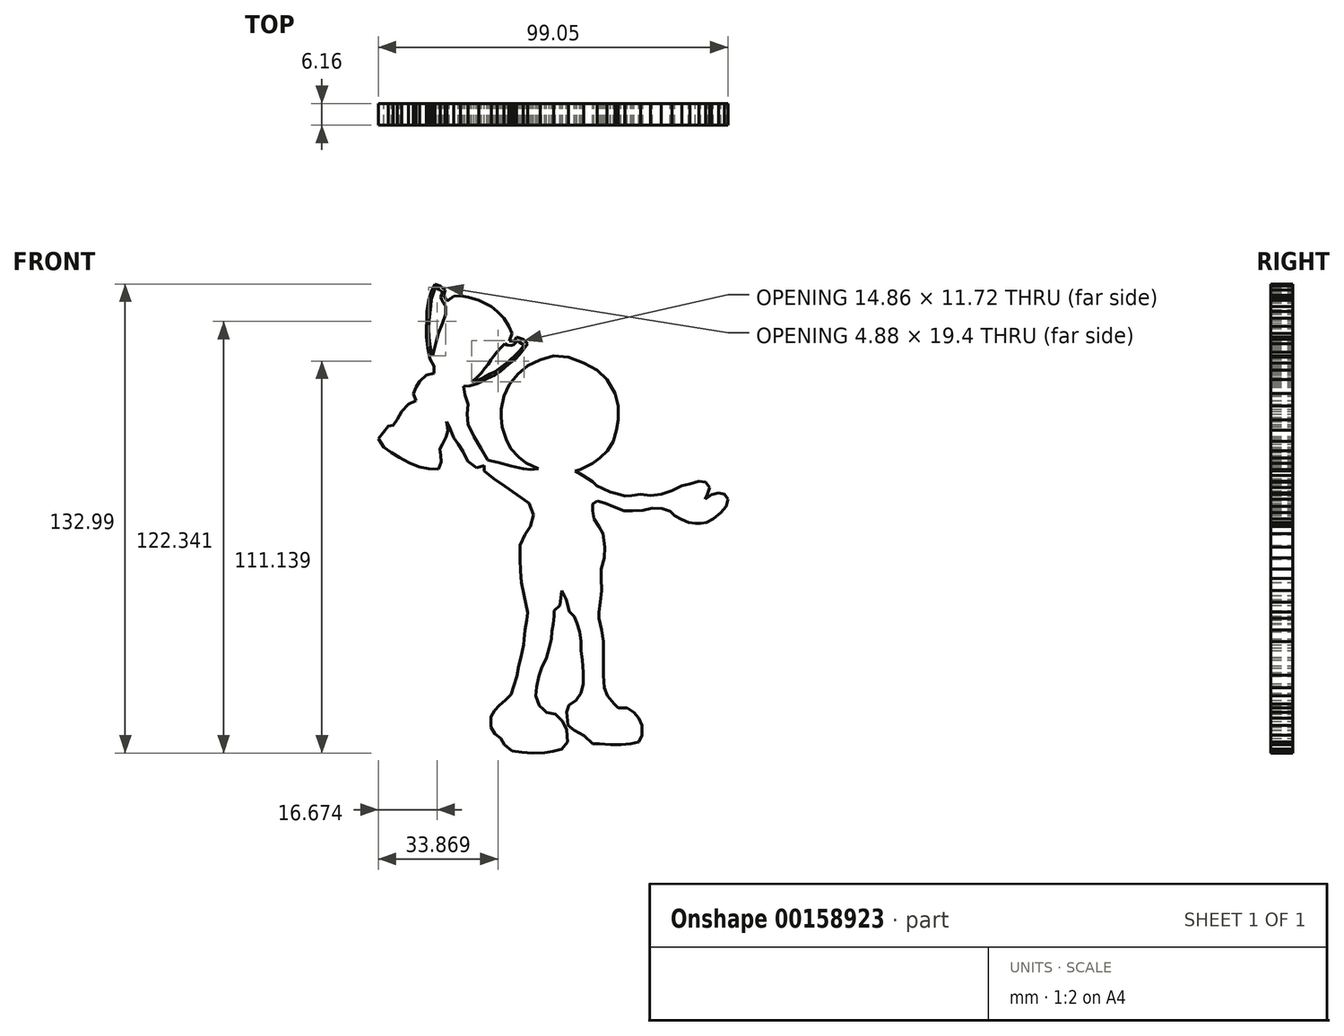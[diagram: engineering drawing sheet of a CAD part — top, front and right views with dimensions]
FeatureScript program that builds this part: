
annotation { "Feature Type Name" : "Feature", "Feature Type Description" : "" }
export const myFeature = defineFeature(function(context is Context, id is Id, definition is map)
    precondition{}
    {
        {
            var Q0;
            Q0=qCreatedBy(makeId("Front.planeOp"),FACE);
            var sketch = newSketch(context, id + "F0", { "sketchPlane" : qUnion([Q0])});
            skLineSegment(sketch, "E0", {"start": v(-2.87, 14.43) * mm, "end": v(0, 12.63) * mm});
            skPoint(sketch, "E1", {"position": v(-19.71, 16.4) * mm});
            skPoint(sketch, "E2", {"position": v(-23.12, 17.11) * mm});
            skPoint(sketch, "E3", {"position": v(-26.88, 18.19) * mm});
            skPoint(sketch, "E4", {"position": v(-29.75, 18.73) * mm});
            skPoint(sketch, "E5", {"position": v(-31.72, 22.13) * mm});
            skPoint(sketch, "E6", {"position": v(-33.69, 25.54) * mm});
            skPoint(sketch, "E7", {"position": v(-35.3, 28.94) * mm});
            skPoint(sketch, "E8", {"position": v(-35.66, 31.8) * mm});
            skPoint(sketch, "E9", {"position": v(-35.3, 34.67) * mm});
            skPoint(sketch, "E10", {"position": v(-36.2, 37.36) * mm});
            skPoint(sketch, "E11", {"position": v(-36.56, 39.7) * mm});
            skPoint(sketch, "E12", {"position": v(-41.04, 27.15) * mm});
            skPoint(sketch, "E13", {"position": v(-39.42, 25.18) * mm});
            skPoint(sketch, "E14", {"position": v(-38.17, 23.38) * mm});
            skPoint(sketch, "E15", {"position": v(-36.73, 21.23) * mm});
            skPoint(sketch, "E16", {"position": v(-35.48, 18.55) * mm});
            skPoint(sketch, "E17", {"position": v(-32.97, 16.58) * mm});
            skPoint(sketch, "E18", {"position": v(-30.82, 17.3) * mm});
            skPoint(sketch, "E19", {"position": v(-30.82, 15.68) * mm});
            skPoint(sketch, "E20", {"position": v(-28.13, 13.53) * mm});
            skPoint(sketch, "E21", {"position": v(-24.9, 11.38) * mm});
            skPoint(sketch, "E22", {"position": v(-21.5, 9.05) * mm});
            skPoint(sketch, "E23", {"position": v(-18.1, 6.54) * mm});
            skPoint(sketch, "E24", {"position": v(-16.84, 3.32) * mm});
            skPoint(sketch, "E25", {"position": v(-17.74, 0) * mm});
            skPoint(sketch, "E26", {"position": v(-19.17, -2.24) * mm});
            skPoint(sketch, "E27", {"position": v(-20.6, -5.29) * mm});
            skPoint(sketch, "E28", {"position": v(-20.6, -9.23) * mm});
            skPoint(sketch, "E29", {"position": v(-20.43, -12.63) * mm});
            skPoint(sketch, "E30", {"position": v(-20.25, -15.86) * mm});
            skPoint(sketch, "E31", {"position": v(-19.53, -19.62) * mm});
            skPoint(sketch, "E32", {"position": v(-18.46, -24.46) * mm});
            skPoint(sketch, "E33", {"position": v(-16.13, -24.46) * mm});
            skPoint(sketch, "E34", {"position": v(-13.62, -23.92) * mm});
            skPoint(sketch, "E35", {"position": v(-10.93, -23.92) * mm});
            skPoint(sketch, "E36", {"position": v(-9.32, -22.3) * mm});
            skPoint(sketch, "E37", {"position": v(-8.78, -18.19) * mm});
            skPoint(sketch, "E38", {"position": v(-7.53, -20.7) * mm});
            skPoint(sketch, "E39", {"position": v(-6.63, -24.1) * mm});
            skPoint(sketch, "E40", {"position": v(-5.2, -25.54) * mm});
            skPoint(sketch, "E41", {"position": v(-3.4, -24.64) * mm});
            skPoint(sketch, "E42", {"position": v(0, -24.1) * mm});
            skPoint(sketch, "E43", {"position": v(1.8, -24.28) * mm});
            skPoint(sketch, "E44", {"position": v(2.15, -21.41) * mm});
            skPoint(sketch, "E45", {"position": v(2.5, -18.19) * mm});
            skPoint(sketch, "E46", {"position": v(2.33, -14.78) * mm});
            skPoint(sketch, "E47", {"position": v(2.33, -12.1) * mm});
            skPoint(sketch, "E48", {"position": v(3.23, -8.87) * mm});
            skPoint(sketch, "E49", {"position": v(3.4, -5.82) * mm});
            skPoint(sketch, "E50", {"position": v(2.87, -2.06) * mm});
            skPoint(sketch, "E51", {"position": v(1.7, 0) * mm});
            skPoint(sketch, "E52", {"position": v(0, 4.38) * mm});
            skPoint(sketch, "E53", {"position": v(0, 6.38) * mm});
            skPoint(sketch, "E54", {"position": v(1.19, 7.18) * mm});
            skPoint(sketch, "E55", {"position": v(3.49, 6.58) * mm});
            skPoint(sketch, "E56", {"position": v(5.99, 5.58) * mm});
            skPoint(sketch, "E57", {"position": v(7.99, 5.38) * mm});
            skPoint(sketch, "E58", {"position": v(7.99, 6.98) * mm});
            skPoint(sketch, "E59", {"position": v(9.09, 8.58) * mm});
            skPoint(sketch, "E60", {"position": v(8.89, 4.48) * mm});
            skPoint(sketch, "E61", {"position": v(11.29, 4.38) * mm});
            skPoint(sketch, "E62", {"position": v(14.19, 4.58) * mm});
            skPoint(sketch, "E63", {"position": v(16.89, 5.18) * mm});
            skPoint(sketch, "E64", {"position": v(19.69, 5.08) * mm});
            skPoint(sketch, "E65", {"position": v(21.89, 4.28) * mm});
            skPoint(sketch, "E66", {"position": v(23.19, 3.08) * mm});
            skPoint(sketch, "E67", {"position": v(25.09, 2.08) * mm});
            skPoint(sketch, "E68", {"position": v(27.09, 1.18) * mm});
            skPoint(sketch, "E69", {"position": v(1.09, 11.58) * mm});
            skPoint(sketch, "E70", {"position": v(2.79, 10.78) * mm});
            skPoint(sketch, "E71", {"position": v(4.89, 9.78) * mm});
            skPoint(sketch, "E72", {"position": v(6.89, 9.28) * mm});
            skPoint(sketch, "E73", {"position": v(10.99, 8.78) * mm});
            skPoint(sketch, "E74", {"position": v(13.59, 9.08) * mm});
            skPoint(sketch, "E75", {"position": v(16.39, 8.78) * mm});
            skPoint(sketch, "E76", {"position": v(19.39, 9.08) * mm});
            skPoint(sketch, "E77", {"position": v(22.49, 10.18) * mm});
            skPoint(sketch, "E78", {"position": v(25.19, 11.58) * mm});
            skPoint(sketch, "E79", {"position": v(27.49, 12.08) * mm});
            skPoint(sketch, "E80", {"position": v(30.09, 12.78) * mm});
            skPoint(sketch, "E81", {"position": v(31.99, 12.58) * mm});
            skPoint(sketch, "E82", {"position": v(33.09, 10.98) * mm});
            skPoint(sketch, "E83", {"position": v(32.49, 9.18) * mm});
            skPoint(sketch, "E84", {"position": v(30.69, 7.78) * mm});
            skPoint(sketch, "E85", {"position": v(29.49, 8.48) * mm});
            skPoint(sketch, "E86", {"position": v(31.89, 7.78) * mm});
            skPoint(sketch, "E87", {"position": v(33.59, 8.98) * mm});
            skPoint(sketch, "E88", {"position": v(35.69, 9.48) * mm});
            skPoint(sketch, "E89", {"position": v(37.29, 9.08) * mm});
            skPoint(sketch, "E90", {"position": v(38.29, 7.68) * mm});
            skPoint(sketch, "E91", {"position": v(37.79, 5.68) * mm});
            skPoint(sketch, "E92", {"position": v(36.29, 3.98) * mm});
            skPoint(sketch, "E93", {"position": v(34.19, 2.18) * mm});
            skPoint(sketch, "E94", {"position": v(32.19, 1.18) * mm});
            skPoint(sketch, "E95", {"position": v(28.99, 0.88) * mm});
            skPoint(sketch, "E96", {"position": v(30.59, 0.88) * mm});
            skPoint(sketch, "E97", {"position": v(-18.76, -26.6) * mm});
            skPoint(sketch, "E98", {"position": v(-19.26, -29.3) * mm});
            skPoint(sketch, "E99", {"position": v(-19.46, -32) * mm});
            skPoint(sketch, "E100", {"position": v(-19.56, -33.5) * mm});
            skPoint(sketch, "E101", {"position": v(-20.36, -37.09) * mm});
            skPoint(sketch, "E102", {"position": v(-20.96, -39.48) * mm});
            skPoint(sketch, "E103", {"position": v(-21.45, -42.48) * mm});
            skPoint(sketch, "E104", {"position": v(-22.35, -45.28) * mm});
            skPoint(sketch, "E105", {"position": v(-23.15, -47.67) * mm});
            skPoint(sketch, "E106", {"position": v(-24.75, -49.27) * mm});
            skPoint(sketch, "E107", {"position": v(-26.45, -50.67) * mm});
            skPoint(sketch, "E108", {"position": v(-27.85, -52.27) * mm});
            skPoint(sketch, "E109", {"position": v(-28.84, -53.96) * mm});
            skPoint(sketch, "E110", {"position": v(-28.84, -56.86) * mm});
            skPoint(sketch, "E111", {"position": v(-27.75, -58.86) * mm});
            skPoint(sketch, "E112", {"position": v(-26.05, -60.05) * mm});
            skPoint(sketch, "E113", {"position": v(-25.05, -61.85) * mm});
            skPoint(sketch, "E114", {"position": v(-22.85, -63.65) * mm});
            skPoint(sketch, "E115", {"position": v(-20.16, -64.05) * mm});
            skPoint(sketch, "E116", {"position": v(-17.06, -64.25) * mm});
            skPoint(sketch, "E117", {"position": v(-13.67, -64.15) * mm});
            skPoint(sketch, "E118", {"position": v(-11.37, -63.75) * mm});
            skPoint(sketch, "E119", {"position": v(-8.77, -63.15) * mm});
            skPoint(sketch, "E120", {"position": v(-7.18, -61.15) * mm});
            skPoint(sketch, "E121", {"position": v(-7.38, -57.66) * mm});
            skPoint(sketch, "E122", {"position": v(-8.57, -55.26) * mm});
            skPoint(sketch, "E123", {"position": v(-10.57, -53.26) * mm});
            skPoint(sketch, "E124", {"position": v(-13.17, -52.77) * mm});
            skPoint(sketch, "E125", {"position": v(-14.07, -51.87) * mm});
            skPoint(sketch, "E126", {"position": v(-15.16, -50.77) * mm});
            skPoint(sketch, "E127", {"position": v(-16.16, -48.07) * mm});
            skPoint(sketch, "E128", {"position": v(-15.96, -45.48) * mm});
            skPoint(sketch, "E129", {"position": v(-15.26, -42.38) * mm});
            skPoint(sketch, "E130", {"position": v(-14.46, -40.08) * mm});
            skPoint(sketch, "E131", {"position": v(-13.07, -37.19) * mm});
            skPoint(sketch, "E132", {"position": v(-12.37, -34.5) * mm});
            skPoint(sketch, "E133", {"position": v(-11.77, -31.9) * mm});
            skPoint(sketch, "E134", {"position": v(-11.27, -27.7) * mm});
            skPoint(sketch, "E135", {"position": v(-10.97, -25.4) * mm});
            skPoint(sketch, "E136", {"position": v(-11.57, -29.7) * mm});
            skPoint(sketch, "E137", {"position": v(-4.48, -27.5) * mm});
            skPoint(sketch, "E138", {"position": v(-3.68, -29.9) * mm});
            skPoint(sketch, "E139", {"position": v(-3.28, -32.5) * mm});
            skPoint(sketch, "E140", {"position": v(-3.38, -35.2) * mm});
            skPoint(sketch, "E141", {"position": v(-2.98, -37.89) * mm});
            skPoint(sketch, "E142", {"position": v(-2.68, -41.38) * mm});
            skPoint(sketch, "E143", {"position": v(-2.68, -44.58) * mm});
            skPoint(sketch, "E144", {"position": v(-3.38, -47.27) * mm});
            skPoint(sketch, "E145", {"position": v(-4.78, -49.27) * mm});
            skPoint(sketch, "E146", {"position": v(-6.78, -50.67) * mm});
            skPoint(sketch, "E147", {"position": v(-7.38, -52.57) * mm});
            skPoint(sketch, "E148", {"position": v(-7.08, -56.36) * mm});
            skPoint(sketch, "E149", {"position": v(-5.28, -57.76) * mm});
            skPoint(sketch, "E150", {"position": v(-2.48, -59.36) * mm});
            skPoint(sketch, "E151", {"position": v(0, -61.65) * mm});
            skPoint(sketch, "E152", {"position": v(1.91, -61.65) * mm});
            skPoint(sketch, "E153", {"position": v(5, -61.85) * mm});
            skPoint(sketch, "E154", {"position": v(7.9, -61.85) * mm});
            skPoint(sketch, "E155", {"position": v(10.8, -61.65) * mm});
            skPoint(sketch, "E156", {"position": v(13.1, -61.05) * mm});
            skPoint(sketch, "E157", {"position": v(14, -59.26) * mm});
            skPoint(sketch, "E158", {"position": v(14, -56.36) * mm});
            skPoint(sketch, "E159", {"position": v(13.1, -54.36) * mm});
            skPoint(sketch, "E160", {"position": v(11.6, -52.67) * mm});
            skPoint(sketch, "E161", {"position": v(9.8, -51.47) * mm});
            skPoint(sketch, "E162", {"position": v(7.2, -51.47) * mm});
            skPoint(sketch, "E163", {"position": v(6, -50.37) * mm});
            skPoint(sketch, "E164", {"position": v(4.2, -48.07) * mm});
            skPoint(sketch, "E165", {"position": v(3.3, -45.78) * mm});
            skPoint(sketch, "E166", {"position": v(3, -42.18) * mm});
            skPoint(sketch, "E167", {"position": v(3, -39.48) * mm});
            skPoint(sketch, "E168", {"position": v(3, -35.79) * mm});
            skPoint(sketch, "E169", {"position": v(3, -32.7) * mm});
            skPoint(sketch, "E170", {"position": v(2.51, -29.3) * mm});
            skPoint(sketch, "E171", {"position": v(1.71, -26.1) * mm});
            skLineSegment(sketch, "E172", {"start": v(0, 12.63) * mm, "end": v(1.09, 11.58) * mm});
            skLineSegment(sketch, "E173", {"start": v(1.09, 11.58) * mm, "end": v(2.79, 10.78) * mm});
            skLineSegment(sketch, "E174", {"start": v(2.79, 10.78) * mm, "end": v(4.89, 9.78) * mm});
            skLineSegment(sketch, "E175", {"start": v(4.89, 9.78) * mm, "end": v(6.89, 9.28) * mm});
            skLineSegment(sketch, "E176", {"start": v(6.89, 9.28) * mm, "end": v(9.09, 8.58) * mm});
            skLineSegment(sketch, "E177", {"start": v(9.09, 8.58) * mm, "end": v(10.99, 8.78) * mm});
            skLineSegment(sketch, "E178", {"start": v(10.99, 8.78) * mm, "end": v(13.59, 9.08) * mm});
            skLineSegment(sketch, "E179", {"start": v(13.59, 9.08) * mm, "end": v(16.39, 8.78) * mm});
            skLineSegment(sketch, "E180", {"start": v(16.39, 8.78) * mm, "end": v(19.39, 9.08) * mm});
            skLineSegment(sketch, "E181", {"start": v(19.39, 9.08) * mm, "end": v(22.49, 10.18) * mm});
            skLineSegment(sketch, "E182", {"start": v(22.49, 10.18) * mm, "end": v(25.19, 11.58) * mm});
            skLineSegment(sketch, "E183", {"start": v(25.19, 11.58) * mm, "end": v(27.49, 12.08) * mm});
            skLineSegment(sketch, "E184", {"start": v(27.49, 12.08) * mm, "end": v(30.09, 12.78) * mm});
            skLineSegment(sketch, "E185", {"start": v(30.09, 12.78) * mm, "end": v(31.99, 12.58) * mm});
            skLineSegment(sketch, "E186", {"start": v(31.99, 12.58) * mm, "end": v(33.09, 10.98) * mm});
            skLineSegment(sketch, "E187", {"start": v(33.09, 10.98) * mm, "end": v(32.49, 9.18) * mm});
            skLineSegment(sketch, "E188", {"start": v(32.49, 9.18) * mm, "end": v(31.89, 7.78) * mm});
            skLineSegment(sketch, "E189", {"start": v(31.89, 7.78) * mm, "end": v(30.69, 7.78) * mm});
            skLineSegment(sketch, "E190", {"start": v(30.69, 7.78) * mm, "end": v(29.49, 8.48) * mm});
            skLineSegment(sketch, "E191", {"start": v(31.89, 7.78) * mm, "end": v(33.59, 8.98) * mm});
            skLineSegment(sketch, "E192", {"start": v(33.59, 8.98) * mm, "end": v(35.69, 9.48) * mm});
            skLineSegment(sketch, "E193", {"start": v(35.69, 9.48) * mm, "end": v(37.29, 9.08) * mm});
            skLineSegment(sketch, "E194", {"start": v(37.29, 9.08) * mm, "end": v(38.29, 7.68) * mm});
            skLineSegment(sketch, "E195", {"start": v(38.29, 7.68) * mm, "end": v(37.79, 5.68) * mm});
            skLineSegment(sketch, "E196", {"start": v(37.79, 5.68) * mm, "end": v(36.29, 3.98) * mm});
            skLineSegment(sketch, "E197", {"start": v(36.29, 3.98) * mm, "end": v(34.19, 2.18) * mm});
            skLineSegment(sketch, "E198", {"start": v(34.19, 2.18) * mm, "end": v(32.19, 1.18) * mm});
            skLineSegment(sketch, "E199", {"start": v(32.19, 1.18) * mm, "end": v(30.59, 0.88) * mm});
            skLineSegment(sketch, "E200", {"start": v(30.59, 0.88) * mm, "end": v(28.99, 0.88) * mm});
            skLineSegment(sketch, "E201", {"start": v(28.99, 0.88) * mm, "end": v(27.09, 1.18) * mm});
            skLineSegment(sketch, "E202", {"start": v(27.09, 1.18) * mm, "end": v(25.09, 2.08) * mm});
            skLineSegment(sketch, "E203", {"start": v(25.09, 2.08) * mm, "end": v(23.19, 3.08) * mm});
            skLineSegment(sketch, "E204", {"start": v(23.19, 3.08) * mm, "end": v(21.89, 4.28) * mm});
            skLineSegment(sketch, "E205", {"start": v(21.89, 4.28) * mm, "end": v(19.69, 5.08) * mm});
            skLineSegment(sketch, "E206", {"start": v(19.69, 5.08) * mm, "end": v(16.89, 5.18) * mm});
            skLineSegment(sketch, "E207", {"start": v(16.89, 5.18) * mm, "end": v(14.19, 4.58) * mm});
            skLineSegment(sketch, "E208", {"start": v(14.19, 4.58) * mm, "end": v(11.29, 4.38) * mm});
            skLineSegment(sketch, "E209", {"start": v(11.29, 4.38) * mm, "end": v(8.89, 4.48) * mm});
            skLineSegment(sketch, "E210", {"start": v(8.89, 4.48) * mm, "end": v(7.99, 5.38) * mm});
            skLineSegment(sketch, "E211", {"start": v(7.99, 5.38) * mm, "end": v(7.99, 6.98) * mm});
            skLineSegment(sketch, "E212", {"start": v(7.99, 6.98) * mm, "end": v(9.09, 8.58) * mm});
            skLineSegment(sketch, "E213", {"start": v(8.89, 4.48) * mm, "end": v(5.99, 5.58) * mm});
            skLineSegment(sketch, "E214", {"start": v(5.99, 5.58) * mm, "end": v(3.49, 6.58) * mm});
            skLineSegment(sketch, "E215", {"start": v(3.49, 6.58) * mm, "end": v(1.19, 7.18) * mm});
            skLineSegment(sketch, "E216", {"start": v(1.19, 7.18) * mm, "end": v(0, 6.38) * mm});
            skLineSegment(sketch, "E217", {"start": v(0, 6.38) * mm, "end": v(0, 4.38) * mm});
            skPoint(sketch, "E218", {"position": v(0.37, 2.2) * mm});
            skLineSegment(sketch, "E219", {"start": v(0, 4.38) * mm, "end": v(0.37, 2.2) * mm});
            skLineSegment(sketch, "E220", {"start": v(0.37, 2.2) * mm, "end": v(1.7, 0) * mm});
            skLineSegment(sketch, "E221", {"start": v(1.7, 0) * mm, "end": v(2.87, -2.06) * mm});
            skLineSegment(sketch, "E222", {"start": v(2.87, -2.06) * mm, "end": v(3.4, -5.82) * mm});
            skLineSegment(sketch, "E223", {"start": v(3.4, -5.82) * mm, "end": v(3.23, -8.87) * mm});
            skLineSegment(sketch, "E224", {"start": v(3.23, -8.87) * mm, "end": v(2.33, -12.1) * mm});
            skLineSegment(sketch, "E225", {"start": v(2.33, -12.1) * mm, "end": v(2.33, -14.78) * mm});
            skLineSegment(sketch, "E226", {"start": v(2.33, -14.78) * mm, "end": v(2.5, -18.19) * mm});
            skLineSegment(sketch, "E227", {"start": v(2.5, -18.19) * mm, "end": v(2.15, -21.41) * mm});
            skLineSegment(sketch, "E228", {"start": v(2.15, -21.41) * mm, "end": v(1.8, -24.28) * mm});
            skLineSegment(sketch, "E229", {"start": v(1.8, -24.28) * mm, "end": v(1.71, -26.1) * mm});
            skLineSegment(sketch, "E230", {"start": v(1.71, -26.1) * mm, "end": v(2.51, -29.3) * mm});
            skLineSegment(sketch, "E231", {"start": v(2.51, -29.3) * mm, "end": v(3, -32.7) * mm});
            skLineSegment(sketch, "E232", {"start": v(3, -32.7) * mm, "end": v(3, -35.79) * mm});
            skLineSegment(sketch, "E233", {"start": v(3, -35.79) * mm, "end": v(3, -39.48) * mm});
            skLineSegment(sketch, "E234", {"start": v(3, -39.48) * mm, "end": v(3, -42.18) * mm});
            skLineSegment(sketch, "E235", {"start": v(3, -42.18) * mm, "end": v(3.3, -45.78) * mm});
            skLineSegment(sketch, "E236", {"start": v(3.3, -45.78) * mm, "end": v(4.2, -48.07) * mm});
            skLineSegment(sketch, "E237", {"start": v(4.2, -48.07) * mm, "end": v(6, -50.37) * mm});
            skLineSegment(sketch, "E238", {"start": v(6, -50.37) * mm, "end": v(7.2, -51.47) * mm});
            skLineSegment(sketch, "E239", {"start": v(7.2, -51.47) * mm, "end": v(9.8, -51.47) * mm});
            skLineSegment(sketch, "E240", {"start": v(9.8, -51.47) * mm, "end": v(11.6, -52.67) * mm});
            skLineSegment(sketch, "E241", {"start": v(11.6, -52.67) * mm, "end": v(13.1, -54.36) * mm});
            skLineSegment(sketch, "E242", {"start": v(13.1, -54.36) * mm, "end": v(14, -56.36) * mm});
            skLineSegment(sketch, "E243", {"start": v(14, -56.36) * mm, "end": v(14, -59.26) * mm});
            skLineSegment(sketch, "E244", {"start": v(14, -59.26) * mm, "end": v(13.1, -61.05) * mm});
            skPoint(sketch, "E245", {"position": v(-34.8, 39.87) * mm});
            skPoint(sketch, "E246", {"position": v(-32.7, 40.54) * mm});
            skPoint(sketch, "E247", {"position": v(-30.06, 41.86) * mm});
            skPoint(sketch, "E248", {"position": v(-27.7, 42.91) * mm});
            skPoint(sketch, "E249", {"position": v(-26.24, 43.97) * mm});
            skPoint(sketch, "E250", {"position": v(-23.87, 45.94) * mm});
            skPoint(sketch, "E251", {"position": v(-21.76, 47.66) * mm});
            skPoint(sketch, "E252", {"position": v(-20.18, 49.37) * mm});
            skPoint(sketch, "E253", {"position": v(-18.47, 51.74) * mm});
            skPoint(sketch, "E254", {"position": v(-19.79, 53.06) * mm});
            skPoint(sketch, "E255", {"position": v(-40.47, 37.36) * mm});
            skPoint(sketch, "E256", {"position": v(-39.15, 38.17) * mm});
            skPoint(sketch, "E257", {"position": v(-37.7, 39.36) * mm});
            skPoint(sketch, "E258", {"position": v(-40.6, 35.93) * mm});
            skPoint(sketch, "E259", {"position": v(-40.74, 34.74) * mm});
            skPoint(sketch, "E260", {"position": v(-42.32, 33.82) * mm});
            skPoint(sketch, "E261", {"position": v(-41.26, 32.5) * mm});
            skPoint(sketch, "E262", {"position": v(-41.4, 31.06) * mm});
            skPoint(sketch, "E263", {"position": v(-41.4, 29.74) * mm});
            skPoint(sketch, "E264", {"position": v(-40.74, 28.29) * mm});
            skPoint(sketch, "E265", {"position": v(-41.53, 25.39) * mm});
            skPoint(sketch, "E266", {"position": v(-42.58, 23.41) * mm});
            skPoint(sketch, "E267", {"position": v(-43.37, 21.96) * mm});
            skPoint(sketch, "E268", {"position": v(-43.1, 20.12) * mm});
            skPoint(sketch, "E269", {"position": v(-42.98, 18.27) * mm});
            skPoint(sketch, "E270", {"position": v(-43.77, 16.3) * mm});
            skPoint(sketch, "E271", {"position": v(-46.53, 16.43) * mm});
            skPoint(sketch, "E272", {"position": v(-49.17, 16.83) * mm});
            skPoint(sketch, "E273", {"position": v(-51.94, 18.01) * mm});
            skPoint(sketch, "E274", {"position": v(-54.83, 19.6) * mm});
            skPoint(sketch, "E275", {"position": v(-57.07, 20.9) * mm});
            skPoint(sketch, "E276", {"position": v(-59.18, 22.5) * mm});
            skPoint(sketch, "E277", {"position": v(-60.76, 24.86) * mm});
            skPoint(sketch, "E278", {"position": v(-59.05, 26.05) * mm});
            skPoint(sketch, "E279", {"position": v(-56.55, 25.52) * mm});
            skPoint(sketch, "E280", {"position": v(-53.52, 24.73) * mm});
            skPoint(sketch, "E281", {"position": v(-51.01, 23.41) * mm});
            skPoint(sketch, "E282", {"position": v(-48.64, 21.96) * mm});
            skPoint(sketch, "E283", {"position": v(-45.61, 19.99) * mm});
            skPoint(sketch, "E284", {"position": v(-44.43, 18.67) * mm});
            skPoint(sketch, "E285", {"position": v(-56.55, 28.68) * mm});
            skPoint(sketch, "E286", {"position": v(-58, 28.42) * mm});
            skPoint(sketch, "E287", {"position": v(-54.97, 28.29) * mm});
            skPoint(sketch, "E288", {"position": v(-52.46, 27.5) * mm});
            skPoint(sketch, "E289", {"position": v(-49.96, 26.05) * mm});
            skPoint(sketch, "E290", {"position": v(-46.67, 24.07) * mm});
            skPoint(sketch, "E291", {"position": v(-55.36, 30.4) * mm});
            skPoint(sketch, "E292", {"position": v(-54.18, 32.64) * mm});
            skPoint(sketch, "E293", {"position": v(-52.2, 34.61) * mm});
            skPoint(sketch, "E294", {"position": v(-50.1, 34.35) * mm});
            skPoint(sketch, "E295", {"position": v(-47.59, 33.56) * mm});
            skPoint(sketch, "E296", {"position": v(-44.43, 31.85) * mm});
            skPoint(sketch, "E297", {"position": v(-49.43, 35.93) * mm});
            skPoint(sketch, "E298", {"position": v(-46.8, 36.72) * mm});
            skPoint(sketch, "E299", {"position": v(-46.14, 38.43) * mm});
            skPoint(sketch, "E300", {"position": v(-44.43, 39.36) * mm});
            skPoint(sketch, "E301", {"position": v(-43.63, 40.94) * mm});
            skPoint(sketch, "E302", {"position": v(-43.63, 43.05) * mm});
            skPoint(sketch, "E303", {"position": v(-44.95, 43.44) * mm});
            skPoint(sketch, "E304", {"position": v(-44.95, 45.42) * mm});
            skPoint(sketch, "E305", {"position": v(-46.14, 47.53) * mm});
            skPoint(sketch, "E306", {"position": v(-46.8, 50.69) * mm});
            skPoint(sketch, "E307", {"position": v(-47.2, 53.72) * mm});
            skPoint(sketch, "E308", {"position": v(-47.2, 56.22) * mm});
            skPoint(sketch, "E309", {"position": v(-47.06, 58.6) * mm});
            skPoint(sketch, "E310", {"position": v(-47.06, 60.96) * mm});
            skPoint(sketch, "E311", {"position": v(-46.53, 64.13) * mm});
            skPoint(sketch, "E312", {"position": v(-45.61, 66.9) * mm});
            skPoint(sketch, "E313", {"position": v(-44.69, 68.74) * mm});
            skPoint(sketch, "E314", {"position": v(-43.24, 68.21) * mm});
            skPoint(sketch, "E315", {"position": v(-41.8, 67.03) * mm});
            skPoint(sketch, "E316", {"position": v(-42.19, 65.58) * mm});
            skPoint(sketch, "E317", {"position": v(-41.26, 63.86) * mm});
            skPoint(sketch, "E318", {"position": v(-39.42, 65.31) * mm});
            skPoint(sketch, "E319", {"position": v(-35.33, 65.05) * mm});
            skPoint(sketch, "E320", {"position": v(-32.3, 64.13) * mm});
            skPoint(sketch, "E321", {"position": v(-28.75, 62.28) * mm});
            skPoint(sketch, "E322", {"position": v(-37.44, 65.44) * mm});
            skPoint(sketch, "E323", {"position": v(-27.03, 60.96) * mm});
            skPoint(sketch, "E324", {"position": v(-25.19, 58.99) * mm});
            skPoint(sketch, "E325", {"position": v(-23.74, 56.75) * mm});
            skPoint(sketch, "E326", {"position": v(-22.95, 54.77) * mm});
            skPoint(sketch, "E327", {"position": v(-23.6, 52.53) * mm});
            skPoint(sketch, "E328", {"position": v(-22.16, 52.53) * mm});
            skPoint(sketch, "E329", {"position": v(-21.63, 53.72) * mm});
            skPoint(sketch, "E330", {"position": v(-41.66, 43.05) * mm});
            skPoint(sketch, "E331", {"position": v(-40.34, 42) * mm});
            skPoint(sketch, "E332", {"position": v(-38.5, 40.94) * mm});
            skPoint(sketch, "E333", {"position": v(-45.36, 48.4) * mm});
            skPoint(sketch, "E334", {"position": v(-44.3, 52.4) * mm});
            skPoint(sketch, "E335", {"position": v(-43.77, 54.9) * mm});
            skPoint(sketch, "E336", {"position": v(-42.58, 57.67) * mm});
            skPoint(sketch, "E337", {"position": v(-41.66, 60.17) * mm});
            skLineSegment(sketch, "E338", {"start": v(13.1, -61.05) * mm, "end": v(10.8, -61.65) * mm});
            skLineSegment(sketch, "E339", {"start": v(10.8, -61.65) * mm, "end": v(7.9, -61.85) * mm});
            skLineSegment(sketch, "E340", {"start": v(5, -61.85) * mm, "end": v(7.9, -61.85) * mm});
            skLineSegment(sketch, "E341", {"start": v(1.91, -61.65) * mm, "end": v(5, -61.85) * mm});
            skLineSegment(sketch, "E342", {"start": v(1.91, -61.65) * mm, "end": v(0, -61.65) * mm});
            skLineSegment(sketch, "E343", {"start": v(0, -61.65) * mm, "end": v(-2.48, -59.36) * mm});
            skLineSegment(sketch, "E344", {"start": v(-2.48, -59.36) * mm, "end": v(-5.28, -57.76) * mm});
            skLineSegment(sketch, "E345", {"start": v(-5.28, -57.76) * mm, "end": v(-7.08, -56.36) * mm});
            skLineSegment(sketch, "E346", {"start": v(-7.08, -56.36) * mm, "end": v(-7.38, -52.57) * mm});
            skLineSegment(sketch, "E347", {"start": v(-7.38, -52.57) * mm, "end": v(-6.78, -50.67) * mm});
            skLineSegment(sketch, "E348", {"start": v(-6.78, -50.67) * mm, "end": v(-4.78, -49.27) * mm});
            skLineSegment(sketch, "E349", {"start": v(-4.78, -49.27) * mm, "end": v(-3.38, -47.27) * mm});
            skLineSegment(sketch, "E350", {"start": v(-3.38, -47.27) * mm, "end": v(-2.68, -44.58) * mm});
            skLineSegment(sketch, "E351", {"start": v(-2.68, -41.38) * mm, "end": v(-2.68, -44.58) * mm});
            skLineSegment(sketch, "E352", {"start": v(-2.98, -37.89) * mm, "end": v(-2.68, -41.38) * mm});
            skLineSegment(sketch, "E353", {"start": v(-3.38, -35.2) * mm, "end": v(-2.98, -37.89) * mm});
            skLineSegment(sketch, "E354", {"start": v(-3.28, -32.5) * mm, "end": v(-3.38, -35.2) * mm});
            skLineSegment(sketch, "E355", {"start": v(-3.68, -29.9) * mm, "end": v(-3.28, -32.5) * mm});
            skLineSegment(sketch, "E356", {"start": v(-4.48, -27.5) * mm, "end": v(-3.68, -29.9) * mm});
            skLineSegment(sketch, "E357", {"start": v(-5.2, -25.54) * mm, "end": v(-4.48, -27.5) * mm});
            skLineSegment(sketch, "E358", {"start": v(-3.4, -24.64) * mm, "end": v(-5.2, -25.54) * mm});
            skLineSegment(sketch, "E359", {"start": v(0, -24.1) * mm, "end": v(-3.4, -24.64) * mm});
            skLineSegment(sketch, "E360", {"start": v(1.8, -24.28) * mm, "end": v(0, -24.1) * mm});
            skLineSegment(sketch, "E361", {"start": v(-6.63, -24.1) * mm, "end": v(-5.2, -25.54) * mm});
            skLineSegment(sketch, "E362", {"start": v(-7.53, -20.7) * mm, "end": v(-6.63, -24.1) * mm});
            skLineSegment(sketch, "E363", {"start": v(-8.78, -18.19) * mm, "end": v(-7.53, -20.7) * mm});
            skLineSegment(sketch, "E364", {"start": v(-8.78, -18.19) * mm, "end": v(-9.32, -22.3) * mm});
            skLineSegment(sketch, "E365", {"start": v(-9.32, -22.3) * mm, "end": v(-10.93, -23.92) * mm});
            skLineSegment(sketch, "E366", {"start": v(-13.62, -23.92) * mm, "end": v(-10.93, -23.92) * mm});
            skLineSegment(sketch, "E367", {"start": v(-16.13, -24.46) * mm, "end": v(-13.62, -23.92) * mm});
            skLineSegment(sketch, "E368", {"start": v(-18.46, -24.46) * mm, "end": v(-16.13, -24.46) * mm});
            skLineSegment(sketch, "E369", {"start": v(-10.93, -23.92) * mm, "end": v(-10.97, -25.4) * mm});
            skLineSegment(sketch, "E370", {"start": v(-10.97, -25.4) * mm, "end": v(-11.27, -27.7) * mm});
            skLineSegment(sketch, "E371", {"start": v(-11.57, -29.7) * mm, "end": v(-11.27, -27.7) * mm});
            skLineSegment(sketch, "E372", {"start": v(-11.77, -31.9) * mm, "end": v(-11.57, -29.7) * mm});
            skLineSegment(sketch, "E373", {"start": v(-12.37, -34.5) * mm, "end": v(-11.77, -31.9) * mm});
            skLineSegment(sketch, "E374", {"start": v(-13.07, -37.19) * mm, "end": v(-12.37, -34.5) * mm});
            skLineSegment(sketch, "E375", {"start": v(-14.46, -40.08) * mm, "end": v(-13.07, -37.19) * mm});
            skLineSegment(sketch, "E376", {"start": v(-15.26, -42.38) * mm, "end": v(-14.46, -40.08) * mm});
            skLineSegment(sketch, "E377", {"start": v(-15.96, -45.48) * mm, "end": v(-15.26, -42.38) * mm});
            skLineSegment(sketch, "E378", {"start": v(-16.16, -48.07) * mm, "end": v(-15.96, -45.48) * mm});
            skLineSegment(sketch, "E379", {"start": v(-15.16, -50.77) * mm, "end": v(-16.16, -48.07) * mm});
            skLineSegment(sketch, "E380", {"start": v(-14.07, -51.87) * mm, "end": v(-15.16, -50.77) * mm});
            skLineSegment(sketch, "E381", {"start": v(-13.17, -52.77) * mm, "end": v(-14.07, -51.87) * mm});
            skLineSegment(sketch, "E382", {"start": v(-10.57, -53.26) * mm, "end": v(-13.17, -52.77) * mm});
            skLineSegment(sketch, "E383", {"start": v(-8.57, -55.26) * mm, "end": v(-10.57, -53.26) * mm});
            skLineSegment(sketch, "E384", {"start": v(-7.38, -57.66) * mm, "end": v(-8.57, -55.26) * mm});
            skLineSegment(sketch, "E385", {"start": v(-7.18, -61.15) * mm, "end": v(-7.38, -57.66) * mm});
            skLineSegment(sketch, "E386", {"start": v(-8.77, -63.15) * mm, "end": v(-7.18, -61.15) * mm});
            skLineSegment(sketch, "E387", {"start": v(-11.37, -63.75) * mm, "end": v(-8.77, -63.15) * mm});
            skLineSegment(sketch, "E388", {"start": v(-13.67, -64.15) * mm, "end": v(-11.37, -63.75) * mm});
            skLineSegment(sketch, "E389", {"start": v(-17.06, -64.25) * mm, "end": v(-13.67, -64.15) * mm});
            skLineSegment(sketch, "E390", {"start": v(-20.16, -64.05) * mm, "end": v(-17.06, -64.25) * mm});
            skLineSegment(sketch, "E391", {"start": v(-22.85, -63.65) * mm, "end": v(-20.16, -64.05) * mm});
            skLineSegment(sketch, "E392", {"start": v(-25.05, -61.85) * mm, "end": v(-22.85, -63.65) * mm});
            skLineSegment(sketch, "E393", {"start": v(-26.05, -60.05) * mm, "end": v(-25.05, -61.85) * mm});
            skLineSegment(sketch, "E394", {"start": v(-27.75, -58.86) * mm, "end": v(-26.05, -60.05) * mm});
            skLineSegment(sketch, "E395", {"start": v(-28.84, -56.86) * mm, "end": v(-27.75, -58.86) * mm});
            skLineSegment(sketch, "E396", {"start": v(-28.84, -53.96) * mm, "end": v(-28.84, -56.86) * mm});
            skLineSegment(sketch, "E397", {"start": v(-27.85, -52.27) * mm, "end": v(-28.84, -53.96) * mm});
            skLineSegment(sketch, "E398", {"start": v(-26.45, -50.67) * mm, "end": v(-27.85, -52.27) * mm});
            skLineSegment(sketch, "E399", {"start": v(-24.75, -49.27) * mm, "end": v(-26.45, -50.67) * mm});
            skLineSegment(sketch, "E400", {"start": v(-23.15, -47.67) * mm, "end": v(-24.75, -49.27) * mm});
            skLineSegment(sketch, "E401", {"start": v(-22.35, -45.28) * mm, "end": v(-23.15, -47.67) * mm});
            skLineSegment(sketch, "E402", {"start": v(-21.45, -42.48) * mm, "end": v(-22.35, -45.28) * mm});
            skLineSegment(sketch, "E403", {"start": v(-20.96, -39.48) * mm, "end": v(-21.45, -42.48) * mm});
            skLineSegment(sketch, "E404", {"start": v(-20.36, -37.09) * mm, "end": v(-20.96, -39.48) * mm});
            skLineSegment(sketch, "E405", {"start": v(-19.56, -33.5) * mm, "end": v(-20.36, -37.09) * mm});
            skLineSegment(sketch, "E406", {"start": v(-19.46, -32) * mm, "end": v(-19.56, -33.5) * mm});
            skLineSegment(sketch, "E407", {"start": v(-19.26, -29.3) * mm, "end": v(-19.46, -32) * mm});
            skLineSegment(sketch, "E408", {"start": v(-18.76, -26.6) * mm, "end": v(-19.26, -29.3) * mm});
            skLineSegment(sketch, "E409", {"start": v(-18.46, -24.46) * mm, "end": v(-18.76, -26.6) * mm});
            skLineSegment(sketch, "E410", {"start": v(-19.53, -19.62) * mm, "end": v(-18.46, -24.46) * mm});
            skLineSegment(sketch, "E411", {"start": v(-20.25, -15.86) * mm, "end": v(-19.53, -19.62) * mm});
            skLineSegment(sketch, "E412", {"start": v(-20.43, -12.63) * mm, "end": v(-20.25, -15.86) * mm});
            skLineSegment(sketch, "E413", {"start": v(-20.6, -9.23) * mm, "end": v(-20.43, -12.63) * mm});
            skLineSegment(sketch, "E414", {"start": v(-20.6, -5.29) * mm, "end": v(-20.6, -9.23) * mm});
            skLineSegment(sketch, "E415", {"start": v(-19.17, -2.24) * mm, "end": v(-20.6, -5.29) * mm});
            skLineSegment(sketch, "E416", {"start": v(-17.74, 0) * mm, "end": v(-19.17, -2.24) * mm});
            skLineSegment(sketch, "E417", {"start": v(-16.84, 3.32) * mm, "end": v(-17.74, 0) * mm});
            skLineSegment(sketch, "E418", {"start": v(-18.1, 6.54) * mm, "end": v(-16.84, 3.32) * mm});
            skLineSegment(sketch, "E419", {"start": v(-21.5, 9.05) * mm, "end": v(-18.1, 6.54) * mm});
            skLineSegment(sketch, "E420", {"start": v(-24.9, 11.38) * mm, "end": v(-21.5, 9.05) * mm});
            skLineSegment(sketch, "E421", {"start": v(-28.13, 13.53) * mm, "end": v(-24.9, 11.38) * mm});
            skLineSegment(sketch, "E422", {"start": v(-30.82, 15.68) * mm, "end": v(-28.13, 13.53) * mm});
            skLineSegment(sketch, "E423", {"start": v(-30.82, 17.3) * mm, "end": v(-30.82, 15.68) * mm});
            skLineSegment(sketch, "E424", {"start": v(-32.97, 16.58) * mm, "end": v(-30.82, 17.3) * mm});
            skLineSegment(sketch, "E425", {"start": v(-29.75, 18.73) * mm, "end": v(-30.82, 17.3) * mm});
            skLineSegment(sketch, "E426", {"start": v(-32.97, 16.58) * mm, "end": v(-35.48, 18.55) * mm});
            skLineSegment(sketch, "E427", {"start": v(-36.73, 21.23) * mm, "end": v(-35.48, 18.55) * mm});
            skLineSegment(sketch, "E428", {"start": v(-38.17, 23.38) * mm, "end": v(-36.73, 21.23) * mm});
            skLineSegment(sketch, "E429", {"start": v(-39.42, 25.18) * mm, "end": v(-38.17, 23.38) * mm});
            skLineSegment(sketch, "E430", {"start": v(-40.74, 28.29) * mm, "end": v(-39.42, 25.18) * mm});
            skPoint(sketch, "E431", {"position": v(-17.6, 16.08) * mm});
            skPoint(sketch, "E432", {"position": v(-15.36, 16.34) * mm});
            skPoint(sketch, "E433", {"position": v(-12.86, 16.74) * mm});
            skPoint(sketch, "E434", {"position": v(-9.7, 16.74) * mm});
            skPoint(sketch, "E435", {"position": v(-6.8, 16.6) * mm});
            skPoint(sketch, "E436", {"position": v(-4.97, 15.68) * mm});
            skPoint(sketch, "E437", {"position": v(-3.65, 16.08) * mm});
            skPoint(sketch, "E438", {"position": v(-2.07, 16.87) * mm});
            skPoint(sketch, "E439", {"position": v(0, 17.92) * mm});
            skPoint(sketch, "E440", {"position": v(2, 19.37) * mm});
            skPoint(sketch, "E441", {"position": v(4.11, 21.47) * mm});
            skPoint(sketch, "E442", {"position": v(5.82, 24.1) * mm});
            skPoint(sketch, "E443", {"position": v(6.74, 27.26) * mm});
            skPoint(sketch, "E444", {"position": v(7.27, 30.16) * mm});
            skPoint(sketch, "E445", {"position": v(7.27, 34.1) * mm});
            skPoint(sketch, "E446", {"position": v(6.35, 37.66) * mm});
            skPoint(sketch, "E447", {"position": v(3.98, 41.6) * mm});
            skPoint(sketch, "E448", {"position": v(1.22, 44.37) * mm});
            skPoint(sketch, "E449", {"position": v(-2.54, 46.3) * mm});
            skPoint(sketch, "E450", {"position": v(-6.87, 48.01) * mm});
            skPoint(sketch, "E451", {"position": v(-11.07, 48.4) * mm});
            skPoint(sketch, "E452", {"position": v(-14.87, 47.22) * mm});
            skPoint(sketch, "E453", {"position": v(-18.42, 45.52) * mm});
            skPoint(sketch, "E454", {"position": v(-21.3, 43.16) * mm});
            skPoint(sketch, "E455", {"position": v(-23.66, 40.27) * mm});
            skPoint(sketch, "E456", {"position": v(-25.24, 37) * mm});
            skPoint(sketch, "E457", {"position": v(-25.9, 33.32) * mm});
            skPoint(sketch, "E458", {"position": v(-25.9, 30.96) * mm});
            skPoint(sketch, "E459", {"position": v(-25.63, 28.2) * mm});
            skPoint(sketch, "E460", {"position": v(-24.58, 24.8) * mm});
            skPoint(sketch, "E461", {"position": v(-23.27, 22.04) * mm});
            skPoint(sketch, "E462", {"position": v(-21.04, 19.67) * mm});
            skPoint(sketch, "E463", {"position": v(-18.94, 17.97) * mm});
            skLineSegment(sketch, "E464", {"start": v(-4.97, 15.68) * mm, "end": v(-2.87, 14.43) * mm});
            skLineSegment(sketch, "E465", {"start": v(-6.8, 16.6) * mm, "end": v(-4.97, 15.68) * mm});
            skLineSegment(sketch, "E466", {"start": v(-9.7, 16.74) * mm, "end": v(-6.8, 16.6) * mm});
            skLineSegment(sketch, "E467", {"start": v(-12.86, 16.74) * mm, "end": v(-9.7, 16.74) * mm});
            skLineSegment(sketch, "E468", {"start": v(-15.36, 16.34) * mm, "end": v(-12.86, 16.74) * mm});
            skLineSegment(sketch, "E469", {"start": v(-17.6, 16.08) * mm, "end": v(-15.36, 16.34) * mm});
            skLineSegment(sketch, "E470", {"start": v(-19.71, 16.4) * mm, "end": v(-17.6, 16.08) * mm});
            skLineSegment(sketch, "E471", {"start": v(-23.12, 17.11) * mm, "end": v(-19.71, 16.4) * mm});
            skLineSegment(sketch, "E472", {"start": v(-26.88, 18.19) * mm, "end": v(-23.12, 17.11) * mm});
            skLineSegment(sketch, "E473", {"start": v(-29.75, 18.73) * mm, "end": v(-26.88, 18.19) * mm});
            skLineSegment(sketch, "E474", {"start": v(-31.72, 22.13) * mm, "end": v(-29.75, 18.73) * mm});
            skLineSegment(sketch, "E475", {"start": v(-33.69, 25.54) * mm, "end": v(-31.72, 22.13) * mm});
            skLineSegment(sketch, "E476", {"start": v(-35.3, 28.94) * mm, "end": v(-33.69, 25.54) * mm});
            skLineSegment(sketch, "E477", {"start": v(-35.66, 31.8) * mm, "end": v(-35.3, 28.94) * mm});
            skLineSegment(sketch, "E478", {"start": v(-35.3, 34.67) * mm, "end": v(-35.66, 31.8) * mm});
            skLineSegment(sketch, "E479", {"start": v(-36.2, 37.36) * mm, "end": v(-35.3, 34.67) * mm});
            skLineSegment(sketch, "E480", {"start": v(-18.94, 17.97) * mm, "end": v(-15.36, 16.34) * mm});
            skLineSegment(sketch, "E481", {"start": v(-21.04, 19.67) * mm, "end": v(-18.94, 17.97) * mm});
            skLineSegment(sketch, "E482", {"start": v(-23.27, 22.04) * mm, "end": v(-21.04, 19.67) * mm});
            skLineSegment(sketch, "E483", {"start": v(-24.58, 24.8) * mm, "end": v(-23.27, 22.04) * mm});
            skLineSegment(sketch, "E484", {"start": v(-25.63, 28.2) * mm, "end": v(-24.58, 24.8) * mm});
            skLineSegment(sketch, "E485", {"start": v(-25.9, 30.96) * mm, "end": v(-25.63, 28.2) * mm});
            skLineSegment(sketch, "E486", {"start": v(-25.9, 33.32) * mm, "end": v(-25.9, 30.96) * mm});
            skLineSegment(sketch, "E487", {"start": v(-25.24, 37) * mm, "end": v(-25.9, 33.32) * mm});
            skLineSegment(sketch, "E488", {"start": v(-23.66, 40.27) * mm, "end": v(-25.24, 37) * mm});
            skLineSegment(sketch, "E489", {"start": v(-21.3, 43.16) * mm, "end": v(-23.66, 40.27) * mm});
            skLineSegment(sketch, "E490", {"start": v(-18.42, 45.52) * mm, "end": v(-21.3, 43.16) * mm});
            skLineSegment(sketch, "E491", {"start": v(-14.87, 47.22) * mm, "end": v(-18.42, 45.52) * mm});
            skLineSegment(sketch, "E492", {"start": v(-11.07, 48.4) * mm, "end": v(-14.87, 47.22) * mm});
            skLineSegment(sketch, "E493", {"start": v(-6.87, 48.01) * mm, "end": v(-11.07, 48.4) * mm});
            skLineSegment(sketch, "E494", {"start": v(-2.54, 46.3) * mm, "end": v(-6.87, 48.01) * mm});
            skLineSegment(sketch, "E495", {"start": v(1.22, 44.37) * mm, "end": v(-2.54, 46.3) * mm});
            skLineSegment(sketch, "E496", {"start": v(3.98, 41.6) * mm, "end": v(1.22, 44.37) * mm});
            skLineSegment(sketch, "E497", {"start": v(6.35, 37.66) * mm, "end": v(3.98, 41.6) * mm});
            skLineSegment(sketch, "E498", {"start": v(7.27, 34.1) * mm, "end": v(6.35, 37.66) * mm});
            skLineSegment(sketch, "E499", {"start": v(7.27, 30.16) * mm, "end": v(7.27, 34.1) * mm});
            skLineSegment(sketch, "E500", {"start": v(6.74, 27.26) * mm, "end": v(7.27, 30.16) * mm});
            skLineSegment(sketch, "E501", {"start": v(5.82, 24.1) * mm, "end": v(6.74, 27.26) * mm});
            skLineSegment(sketch, "E502", {"start": v(4.11, 21.47) * mm, "end": v(5.82, 24.1) * mm});
            skLineSegment(sketch, "E503", {"start": v(2, 19.37) * mm, "end": v(4.11, 21.47) * mm});
            skLineSegment(sketch, "E504", {"start": v(0, 17.92) * mm, "end": v(2, 19.37) * mm});
            skLineSegment(sketch, "E505", {"start": v(-2.07, 16.87) * mm, "end": v(0, 17.92) * mm});
            skLineSegment(sketch, "E506", {"start": v(-3.65, 16.08) * mm, "end": v(-2.07, 16.87) * mm});
            skLineSegment(sketch, "E507", {"start": v(-4.97, 15.68) * mm, "end": v(-3.65, 16.08) * mm});
            skLineSegment(sketch, "E508", {"start": v(-41.04, 27.15) * mm, "end": v(-41.4, 29.74) * mm});
            skLineSegment(sketch, "E509", {"start": v(-41.4, 31.06) * mm, "end": v(-41.4, 29.74) * mm});
            skLineSegment(sketch, "E510", {"start": v(-41.26, 32.5) * mm, "end": v(-41.4, 31.06) * mm});
            skLineSegment(sketch, "E511", {"start": v(-42.32, 33.82) * mm, "end": v(-41.26, 32.5) * mm});
            skLineSegment(sketch, "E512", {"start": v(-40.74, 34.74) * mm, "end": v(-42.32, 33.82) * mm});
            skLineSegment(sketch, "E513", {"start": v(-40.6, 35.93) * mm, "end": v(-40.74, 34.74) * mm});
            skLineSegment(sketch, "E514", {"start": v(-40.47, 37.36) * mm, "end": v(-40.6, 35.93) * mm});
            skLineSegment(sketch, "E515", {"start": v(-39.15, 38.17) * mm, "end": v(-40.47, 37.36) * mm});
            skLineSegment(sketch, "E516", {"start": v(-37.7, 39.36) * mm, "end": v(-39.15, 38.17) * mm});
            skLineSegment(sketch, "E517", {"start": v(-36.56, 39.7) * mm, "end": v(-37.7, 39.36) * mm});
            skLineSegment(sketch, "E518", {"start": v(-34.8, 39.87) * mm, "end": v(-36.56, 39.7) * mm});
            skLineSegment(sketch, "E519", {"start": v(-32.7, 40.54) * mm, "end": v(-34.8, 39.87) * mm});
            skLineSegment(sketch, "E520", {"start": v(-30.06, 41.86) * mm, "end": v(-32.7, 40.54) * mm});
            skLineSegment(sketch, "E521", {"start": v(-27.7, 42.91) * mm, "end": v(-30.06, 41.86) * mm});
            skLineSegment(sketch, "E522", {"start": v(-26.24, 43.97) * mm, "end": v(-27.7, 42.91) * mm});
            skLineSegment(sketch, "E523", {"start": v(-23.87, 45.94) * mm, "end": v(-26.24, 43.97) * mm});
            skLineSegment(sketch, "E524", {"start": v(-21.76, 47.66) * mm, "end": v(-23.87, 45.94) * mm});
            skLineSegment(sketch, "E525", {"start": v(-20.18, 49.37) * mm, "end": v(-21.76, 47.66) * mm});
            skLineSegment(sketch, "E526", {"start": v(-18.47, 51.74) * mm, "end": v(-20.18, 49.37) * mm});
            skLineSegment(sketch, "E527", {"start": v(-19.79, 53.06) * mm, "end": v(-18.47, 51.74) * mm});
            skLineSegment(sketch, "E528", {"start": v(-21.63, 53.72) * mm, "end": v(-19.79, 53.06) * mm});
            skLineSegment(sketch, "E529", {"start": v(-22.16, 52.53) * mm, "end": v(-21.63, 53.72) * mm});
            skLineSegment(sketch, "E530", {"start": v(-23.6, 52.53) * mm, "end": v(-22.16, 52.53) * mm});
            skLineSegment(sketch, "E531", {"start": v(-22.95, 54.77) * mm, "end": v(-23.6, 52.53) * mm});
            skLineSegment(sketch, "E532", {"start": v(-23.74, 56.75) * mm, "end": v(-22.95, 54.77) * mm});
            skLineSegment(sketch, "E533", {"start": v(-25.19, 58.99) * mm, "end": v(-23.74, 56.75) * mm});
            skLineSegment(sketch, "E534", {"start": v(-27.03, 60.96) * mm, "end": v(-25.19, 58.99) * mm});
            skLineSegment(sketch, "E535", {"start": v(-28.75, 62.28) * mm, "end": v(-27.03, 60.96) * mm});
            skLineSegment(sketch, "E536", {"start": v(-32.3, 64.13) * mm, "end": v(-28.75, 62.28) * mm});
            skLineSegment(sketch, "E537", {"start": v(-35.33, 65.05) * mm, "end": v(-32.3, 64.13) * mm});
            skLineSegment(sketch, "E538", {"start": v(-37.44, 65.44) * mm, "end": v(-35.33, 65.05) * mm});
            skLineSegment(sketch, "E539", {"start": v(-39.42, 65.31) * mm, "end": v(-37.44, 65.44) * mm});
            skLineSegment(sketch, "E540", {"start": v(-41.26, 63.86) * mm, "end": v(-39.42, 65.31) * mm});
            skLineSegment(sketch, "E541", {"start": v(-42.19, 65.58) * mm, "end": v(-41.26, 63.86) * mm});
            skLineSegment(sketch, "E542", {"start": v(-41.8, 67.03) * mm, "end": v(-42.19, 65.58) * mm});
            skLineSegment(sketch, "E543", {"start": v(-43.24, 68.21) * mm, "end": v(-41.8, 67.03) * mm});
            skLineSegment(sketch, "E544", {"start": v(-43.24, 68.21) * mm, "end": v(-44.69, 68.74) * mm});
            skLineSegment(sketch, "E545", {"start": v(-44.69, 68.74) * mm, "end": v(-45.61, 66.9) * mm});
            skLineSegment(sketch, "E546", {"start": v(-45.61, 66.9) * mm, "end": v(-46.53, 64.13) * mm});
            skLineSegment(sketch, "E547", {"start": v(-46.53, 64.13) * mm, "end": v(-47.06, 60.96) * mm});
            skLineSegment(sketch, "E548", {"start": v(-47.06, 60.96) * mm, "end": v(-47.06, 58.6) * mm});
            skLineSegment(sketch, "E549", {"start": v(-47.2, 56.22) * mm, "end": v(-47.06, 58.6) * mm});
            skLineSegment(sketch, "E550", {"start": v(-47.2, 53.72) * mm, "end": v(-47.2, 56.22) * mm});
            skLineSegment(sketch, "E551", {"start": v(-46.8, 50.69) * mm, "end": v(-47.2, 53.72) * mm});
            skLineSegment(sketch, "E552", {"start": v(-46.14, 47.53) * mm, "end": v(-46.8, 50.69) * mm});
            skLineSegment(sketch, "E553", {"start": v(-44.95, 45.42) * mm, "end": v(-46.14, 47.53) * mm});
            skLineSegment(sketch, "E554", {"start": v(-44.95, 43.44) * mm, "end": v(-44.95, 45.42) * mm});
            skLineSegment(sketch, "E555", {"start": v(-43.63, 43.05) * mm, "end": v(-44.95, 43.44) * mm});
            skLineSegment(sketch, "E556", {"start": v(-37.7, 39.36) * mm, "end": v(-38.5, 40.94) * mm});
            skLineSegment(sketch, "E557", {"start": v(-38.5, 40.94) * mm, "end": v(-40.34, 42) * mm});
            skLineSegment(sketch, "E558", {"start": v(-41.66, 43.05) * mm, "end": v(-40.34, 42) * mm});
            skLineSegment(sketch, "E559", {"start": v(-43.63, 43.05) * mm, "end": v(-41.66, 43.05) * mm});
            skLineSegment(sketch, "E560", {"start": v(-43.63, 40.94) * mm, "end": v(-43.63, 43.05) * mm});
            skLineSegment(sketch, "E561", {"start": v(-44.43, 39.36) * mm, "end": v(-43.63, 40.94) * mm});
            skLineSegment(sketch, "E562", {"start": v(-46.14, 38.43) * mm, "end": v(-44.43, 39.36) * mm});
            skLineSegment(sketch, "E563", {"start": v(-46.8, 36.72) * mm, "end": v(-46.14, 38.43) * mm});
            skLineSegment(sketch, "E564", {"start": v(-49.43, 35.93) * mm, "end": v(-46.8, 36.72) * mm});
            skLineSegment(sketch, "E565", {"start": v(-52.2, 34.61) * mm, "end": v(-49.43, 35.93) * mm});
            skLineSegment(sketch, "E566", {"start": v(-50.1, 34.35) * mm, "end": v(-52.2, 34.61) * mm});
            skLineSegment(sketch, "E567", {"start": v(-47.59, 33.56) * mm, "end": v(-50.1, 34.35) * mm});
            skLineSegment(sketch, "E568", {"start": v(-44.43, 31.85) * mm, "end": v(-47.59, 33.56) * mm});
            skLineSegment(sketch, "E569", {"start": v(-41.4, 29.74) * mm, "end": v(-44.43, 31.85) * mm});
            skLineSegment(sketch, "E570", {"start": v(-54.18, 32.64) * mm, "end": v(-52.2, 34.61) * mm});
            skLineSegment(sketch, "E571", {"start": v(-55.36, 30.4) * mm, "end": v(-54.18, 32.64) * mm});
            skLineSegment(sketch, "E572", {"start": v(-56.55, 28.68) * mm, "end": v(-55.36, 30.4) * mm});
            skLineSegment(sketch, "E573", {"start": v(-58, 28.42) * mm, "end": v(-56.55, 28.68) * mm});
            skLineSegment(sketch, "E574", {"start": v(-58, 28.42) * mm, "end": v(-60.76, 24.86) * mm});
            skLineSegment(sketch, "E575", {"start": v(-60.76, 24.86) * mm, "end": v(-59.18, 22.5) * mm});
            skLineSegment(sketch, "E576", {"start": v(-57.07, 20.9) * mm, "end": v(-59.18, 22.5) * mm});
            skLineSegment(sketch, "E577", {"start": v(-54.83, 19.6) * mm, "end": v(-57.07, 20.9) * mm});
            skLineSegment(sketch, "E578", {"start": v(-51.94, 18.01) * mm, "end": v(-54.83, 19.6) * mm});
            skLineSegment(sketch, "E579", {"start": v(-49.17, 16.83) * mm, "end": v(-51.94, 18.01) * mm});
            skLineSegment(sketch, "E580", {"start": v(-46.53, 16.43) * mm, "end": v(-49.17, 16.83) * mm});
            skLineSegment(sketch, "E581", {"start": v(-43.77, 16.3) * mm, "end": v(-46.53, 16.43) * mm});
            skLineSegment(sketch, "E582", {"start": v(-42.98, 18.27) * mm, "end": v(-43.77, 16.3) * mm});
            skLineSegment(sketch, "E583", {"start": v(-43.1, 20.12) * mm, "end": v(-42.98, 18.27) * mm});
            skLineSegment(sketch, "E584", {"start": v(-43.37, 21.96) * mm, "end": v(-43.1, 20.12) * mm});
            skLineSegment(sketch, "E585", {"start": v(-42.58, 23.41) * mm, "end": v(-43.37, 21.96) * mm});
            skLineSegment(sketch, "E586", {"start": v(-41.53, 25.39) * mm, "end": v(-42.58, 23.41) * mm});
            skLineSegment(sketch, "E587", {"start": v(-41.04, 27.15) * mm, "end": v(-41.53, 25.39) * mm});
            skLineSegment(sketch, "E588", {"start": v(-56.55, 28.68) * mm, "end": v(-54.97, 28.29) * mm});
            skLineSegment(sketch, "E589", {"start": v(-52.46, 27.5) * mm, "end": v(-54.97, 28.29) * mm});
            skLineSegment(sketch, "E590", {"start": v(-49.96, 26.05) * mm, "end": v(-52.46, 27.5) * mm});
            skLineSegment(sketch, "E591", {"start": v(-46.67, 24.07) * mm, "end": v(-49.96, 26.05) * mm});
            skLineSegment(sketch, "E592", {"start": v(-43.37, 21.96) * mm, "end": v(-46.67, 24.07) * mm});
            skLineSegment(sketch, "E593", {"start": v(-59.05, 26.05) * mm, "end": v(-56.55, 25.52) * mm});
            skLineSegment(sketch, "E594", {"start": v(-59.05, 26.05) * mm, "end": v(-60.76, 24.86) * mm});
            skLineSegment(sketch, "E595", {"start": v(-53.52, 24.73) * mm, "end": v(-56.55, 25.52) * mm});
            skLineSegment(sketch, "E596", {"start": v(-51.01, 23.41) * mm, "end": v(-53.52, 24.73) * mm});
            skLineSegment(sketch, "E597", {"start": v(-48.64, 21.96) * mm, "end": v(-51.01, 23.41) * mm});
            skLineSegment(sketch, "E598", {"start": v(-45.61, 19.99) * mm, "end": v(-48.64, 21.96) * mm});
            skLineSegment(sketch, "E599", {"start": v(-44.43, 18.67) * mm, "end": v(-45.61, 19.99) * mm});
            skLineSegment(sketch, "E600", {"start": v(-43.77, 16.3) * mm, "end": v(-44.43, 18.67) * mm});
            skLineSegment(sketch, "E601", {"start": v(-41.66, 60.17) * mm, "end": v(-42.58, 57.67) * mm});
            skLineSegment(sketch, "E602", {"start": v(-42.58, 57.67) * mm, "end": v(-43.77, 54.9) * mm});
            skLineSegment(sketch, "E603", {"start": v(-44.3, 52.4) * mm, "end": v(-45.36, 48.4) * mm});
            skLineSegment(sketch, "E604", {"start": v(-43.77, 54.9) * mm, "end": v(-44.3, 52.4) * mm});
            skPoint(sketch, "E605", {"position": v(-47, 52.2) * mm});
            skPoint(sketch, "E606", {"position": v(-46.07, 65.51) * mm});
            skPoint(sketch, "E607", {"position": v(-41.66, 62.51) * mm});
            skPoint(sketch, "E608", {"position": v(-50.1, 39.46) * mm});
            skPoint(sketch, "E609", {"position": v(-49.1, 41.16) * mm});
            skPoint(sketch, "E610", {"position": v(-47.13, 42.86) * mm});
            skPoint(sketch, "E611", {"position": v(-50.8, 37.62) * mm});
            skPoint(sketch, "E612", {"position": v(-50.1, 35.62) * mm});
            skLineSegment(sketch, "E613", {"start": v(-44.95, 43.44) * mm, "end": v(-47.13, 42.86) * mm});
            skLineSegment(sketch, "E614", {"start": v(-49.1, 41.16) * mm, "end": v(-47.13, 42.86) * mm});
            skLineSegment(sketch, "E615", {"start": v(-50.1, 39.46) * mm, "end": v(-49.1, 41.16) * mm});
            skLineSegment(sketch, "E616", {"start": v(-50.8, 37.62) * mm, "end": v(-50.1, 39.46) * mm});
            skLineSegment(sketch, "E617", {"start": v(-50.1, 35.62) * mm, "end": v(-50.8, 37.62) * mm});
            skLineSegment(sketch, "E618", {"start": v(-36.56, 39.7) * mm, "end": v(-36.2, 37.36) * mm});
            skLineSegment(sketch, "E619", {"start": v(-40.74, 28.29) * mm, "end": v(-41.4, 29.74) * mm});
            skPoint(sketch, "E620", {"position": v(-45.87, 50.13) * mm});
            skPoint(sketch, "E621", {"position": v(-46.08, 51.68) * mm});
            skPoint(sketch, "E622", {"position": v(-46.38, 53.72) * mm});
            skPoint(sketch, "E623", {"position": v(-46.52, 56.09) * mm});
            skPoint(sketch, "E624", {"position": v(-46.44, 58.27) * mm});
            skPoint(sketch, "E625", {"position": v(-46.14, 60.43) * mm});
            skPoint(sketch, "E626", {"position": v(-45.93, 62.44) * mm});
            skPoint(sketch, "E627", {"position": v(-45.72, 64.32) * mm});
            skPoint(sketch, "E628", {"position": v(-45.27, 65.94) * mm});
            skPoint(sketch, "E629", {"position": v(-44.6, 67.8) * mm});
            skPoint(sketch, "E630", {"position": v(-43.65, 67.22) * mm});
            skPoint(sketch, "E631", {"position": v(-42.46, 66.39) * mm});
            skPoint(sketch, "E632", {"position": v(-42.81, 65.76) * mm});
            skPoint(sketch, "E633", {"position": v(-43.05, 65) * mm});
            skPoint(sketch, "E634", {"position": v(-42.87, 64.35) * mm});
            skPoint(sketch, "E635", {"position": v(-42.28, 63.34) * mm});
            skPoint(sketch, "E636", {"position": v(-41.65, 61.42) * mm});
            skLineSegment(sketch, "E637", {"start": v(-45.36, 48.4) * mm, "end": v(-45.87, 50.13) * mm});
            skLineSegment(sketch, "E638", {"start": v(-46.08, 51.68) * mm, "end": v(-45.87, 50.13) * mm});
            skLineSegment(sketch, "E639", {"start": v(-46.38, 53.72) * mm, "end": v(-46.08, 51.68) * mm});
            skLineSegment(sketch, "E640", {"start": v(-46.52, 56.09) * mm, "end": v(-46.38, 53.72) * mm});
            skLineSegment(sketch, "E641", {"start": v(-46.44, 58.27) * mm, "end": v(-46.52, 56.09) * mm});
            skLineSegment(sketch, "E642", {"start": v(-46.14, 60.43) * mm, "end": v(-46.44, 58.27) * mm});
            skLineSegment(sketch, "E643", {"start": v(-41.65, 61.42) * mm, "end": v(-41.66, 60.17) * mm});
            skLineSegment(sketch, "E644", {"start": v(-41.66, 62.51) * mm, "end": v(-41.65, 61.42) * mm});
            skLineSegment(sketch, "E645", {"start": v(-42.28, 63.34) * mm, "end": v(-41.66, 62.51) * mm});
            skLineSegment(sketch, "E646", {"start": v(-42.87, 64.35) * mm, "end": v(-42.28, 63.34) * mm});
            skLineSegment(sketch, "E647", {"start": v(-43.05, 65) * mm, "end": v(-42.87, 64.35) * mm});
            skLineSegment(sketch, "E648", {"start": v(-42.81, 65.76) * mm, "end": v(-43.05, 65) * mm});
            skLineSegment(sketch, "E649", {"start": v(-42.46, 66.39) * mm, "end": v(-42.81, 65.76) * mm});
            skLineSegment(sketch, "E650", {"start": v(-44.6, 67.8) * mm, "end": v(-43.65, 67.22) * mm});
            skLineSegment(sketch, "E651", {"start": v(-42.46, 66.39) * mm, "end": v(-43.65, 67.22) * mm});
            skLineSegment(sketch, "E652", {"start": v(-44.6, 67.8) * mm, "end": v(-45.27, 65.94) * mm});
            skLineSegment(sketch, "E653", {"start": v(-45.72, 64.32) * mm, "end": v(-45.27, 65.94) * mm});
            skLineSegment(sketch, "E654", {"start": v(-45.93, 62.44) * mm, "end": v(-45.72, 64.32) * mm});
            skLineSegment(sketch, "E655", {"start": v(-46.14, 60.43) * mm, "end": v(-45.93, 62.44) * mm});
            skPoint(sketch, "E656", {"position": v(-25, 51.76) * mm});
            skPoint(sketch, "E657", {"position": v(-24.24, 51.46) * mm});
            skPoint(sketch, "E658", {"position": v(-23.2, 51.34) * mm});
            skPoint(sketch, "E659", {"position": v(-22.33, 51.55) * mm});
            skPoint(sketch, "E660", {"position": v(-21.58, 52.27) * mm});
            skPoint(sketch, "E661", {"position": v(-21.34, 52.75) * mm});
            skPoint(sketch, "E662", {"position": v(-20.72, 52.21) * mm});
            skPoint(sketch, "E663", {"position": v(-19.46, 51.46) * mm});
            skPoint(sketch, "E664", {"position": v(-20, 50.78) * mm});
            skPoint(sketch, "E665", {"position": v(-20.78, 49.82) * mm});
            skPoint(sketch, "E666", {"position": v(-22.1, 48.32) * mm});
            skPoint(sketch, "E667", {"position": v(-23.44, 47.19) * mm});
            skPoint(sketch, "E668", {"position": v(-24.57, 46.17) * mm});
            skPoint(sketch, "E669", {"position": v(-26.04, 45.07) * mm});
            skPoint(sketch, "E670", {"position": v(-27.62, 43.93) * mm});
            skPoint(sketch, "E671", {"position": v(-29.24, 43.15) * mm});
            skPoint(sketch, "E672", {"position": v(-30.82, 42.28) * mm});
            skPoint(sketch, "E673", {"position": v(-32.38, 41.57) * mm});
            skPoint(sketch, "E674", {"position": v(-34.32, 41.03) * mm});
            skPoint(sketch, "E675", {"position": v(-33.04, 42.02) * mm});
            skPoint(sketch, "E676", {"position": v(-31.57, 43.51) * mm});
            skPoint(sketch, "E677", {"position": v(-30.58, 44.8) * mm});
            skPoint(sketch, "E678", {"position": v(-29.63, 46.02) * mm});
            skPoint(sketch, "E679", {"position": v(-28.82, 47.19) * mm});
            skPoint(sketch, "E680", {"position": v(-28.04, 48.23) * mm});
            skPoint(sketch, "E681", {"position": v(-27.18, 49.37) * mm});
            skPoint(sketch, "E682", {"position": v(-26.13, 50.63) * mm});
            skLineSegment(sketch, "E683", {"start": v(-34.32, 41.03) * mm, "end": v(-32.38, 41.57) * mm});
            skLineSegment(sketch, "E684", {"start": v(-30.82, 42.28) * mm, "end": v(-32.38, 41.57) * mm});
            skLineSegment(sketch, "E685", {"start": v(-29.24, 43.15) * mm, "end": v(-30.82, 42.28) * mm});
            skLineSegment(sketch, "E686", {"start": v(-27.62, 43.93) * mm, "end": v(-29.24, 43.15) * mm});
            skLineSegment(sketch, "E687", {"start": v(-26.04, 45.07) * mm, "end": v(-27.62, 43.93) * mm});
            skLineSegment(sketch, "E688", {"start": v(-24.57, 46.17) * mm, "end": v(-26.04, 45.07) * mm});
            skLineSegment(sketch, "E689", {"start": v(-23.44, 47.19) * mm, "end": v(-24.57, 46.17) * mm});
            skLineSegment(sketch, "E690", {"start": v(-22.1, 48.32) * mm, "end": v(-23.44, 47.19) * mm});
            skLineSegment(sketch, "E691", {"start": v(-20.78, 49.82) * mm, "end": v(-22.1, 48.32) * mm});
            skLineSegment(sketch, "E692", {"start": v(-20, 50.78) * mm, "end": v(-20.78, 49.82) * mm});
            skLineSegment(sketch, "E693", {"start": v(-19.46, 51.46) * mm, "end": v(-20, 50.78) * mm});
            skLineSegment(sketch, "E694", {"start": v(-20.72, 52.21) * mm, "end": v(-19.46, 51.46) * mm});
            skLineSegment(sketch, "E695", {"start": v(-21.34, 52.75) * mm, "end": v(-20.72, 52.21) * mm});
            skLineSegment(sketch, "E696", {"start": v(-21.58, 52.27) * mm, "end": v(-21.34, 52.75) * mm});
            skLineSegment(sketch, "E697", {"start": v(-22.33, 51.55) * mm, "end": v(-21.58, 52.27) * mm});
            skLineSegment(sketch, "E698", {"start": v(-23.2, 51.34) * mm, "end": v(-22.33, 51.55) * mm});
            skLineSegment(sketch, "E699", {"start": v(-24.24, 51.46) * mm, "end": v(-23.2, 51.34) * mm});
            skLineSegment(sketch, "E700", {"start": v(-25, 51.76) * mm, "end": v(-24.24, 51.46) * mm});
            skLineSegment(sketch, "E701", {"start": v(-26.13, 50.63) * mm, "end": v(-25, 51.76) * mm});
            skLineSegment(sketch, "E702", {"start": v(-27.18, 49.37) * mm, "end": v(-26.13, 50.63) * mm});
            skLineSegment(sketch, "E703", {"start": v(-28.04, 48.23) * mm, "end": v(-27.18, 49.37) * mm});
            skLineSegment(sketch, "E704", {"start": v(-28.82, 47.19) * mm, "end": v(-28.04, 48.23) * mm});
            skLineSegment(sketch, "E705", {"start": v(-29.63, 46.02) * mm, "end": v(-28.82, 47.19) * mm});
            skLineSegment(sketch, "E706", {"start": v(-30.58, 44.8) * mm, "end": v(-29.63, 46.02) * mm});
            skLineSegment(sketch, "E707", {"start": v(-31.57, 43.51) * mm, "end": v(-30.58, 44.8) * mm});
            skLineSegment(sketch, "E708", {"start": v(-33.04, 42.02) * mm, "end": v(-31.57, 43.51) * mm});
            skLineSegment(sketch, "E709", {"start": v(-34.32, 41.03) * mm, "end": v(-33.04, 42.02) * mm});
            skSolve(sketch);
        }
        {
            var Q0;
            Q0 = qSketchRegion(id + "F0", true);
            extrude(context, id + "F1", {"entities" : qUnion([Q0]), "depth" : 6.16 * mm});
        }
    });
